# Revit family: DSP_A3-AC-Doors-FDS6
name_source: partatom
category: Doors
revit_build: Autodesk Revit 2016 (Build: 20150220_1215(x64)
units: mm (PartAtom-declared; Revit-internal decimal feet)

## family parameters
Always vertical = Yes
Cut with Voids When Loaded = No
Host = Wall
Room Calculation Point = No
Shared = No

## types (1)
- AC Door
    Frame Depth = 48 mm  [stored 0.15748 ft]
    Frame Material = Meranti Wood
    Frame Width = 102 mm  [stored 0.334646 ft]
    Function = Interior
    Glass Material = Glass
    Glass Thickness = 8 mm  [stored 0.0262467 ft]
    Height = 2080 mm  [stored 6.82415 ft]
    Made by = Tolani Civil Projects cc
    Manufacturer = A3 Architects
    URL = http://www.a3architects.co.za
    URL for TCP = http://www.tcpbim.co.za
    Wall Closure = By host
    Width = 1793 mm  [stored 5.88255 ft]

note: [stored X ft] marks values corroborated as IEEE doubles in the binary element streams (Revit-internal decimal feet)

## geometry (parser evidence)
native form markers: Sweep x2
no freeform markers — native parametric forms only
